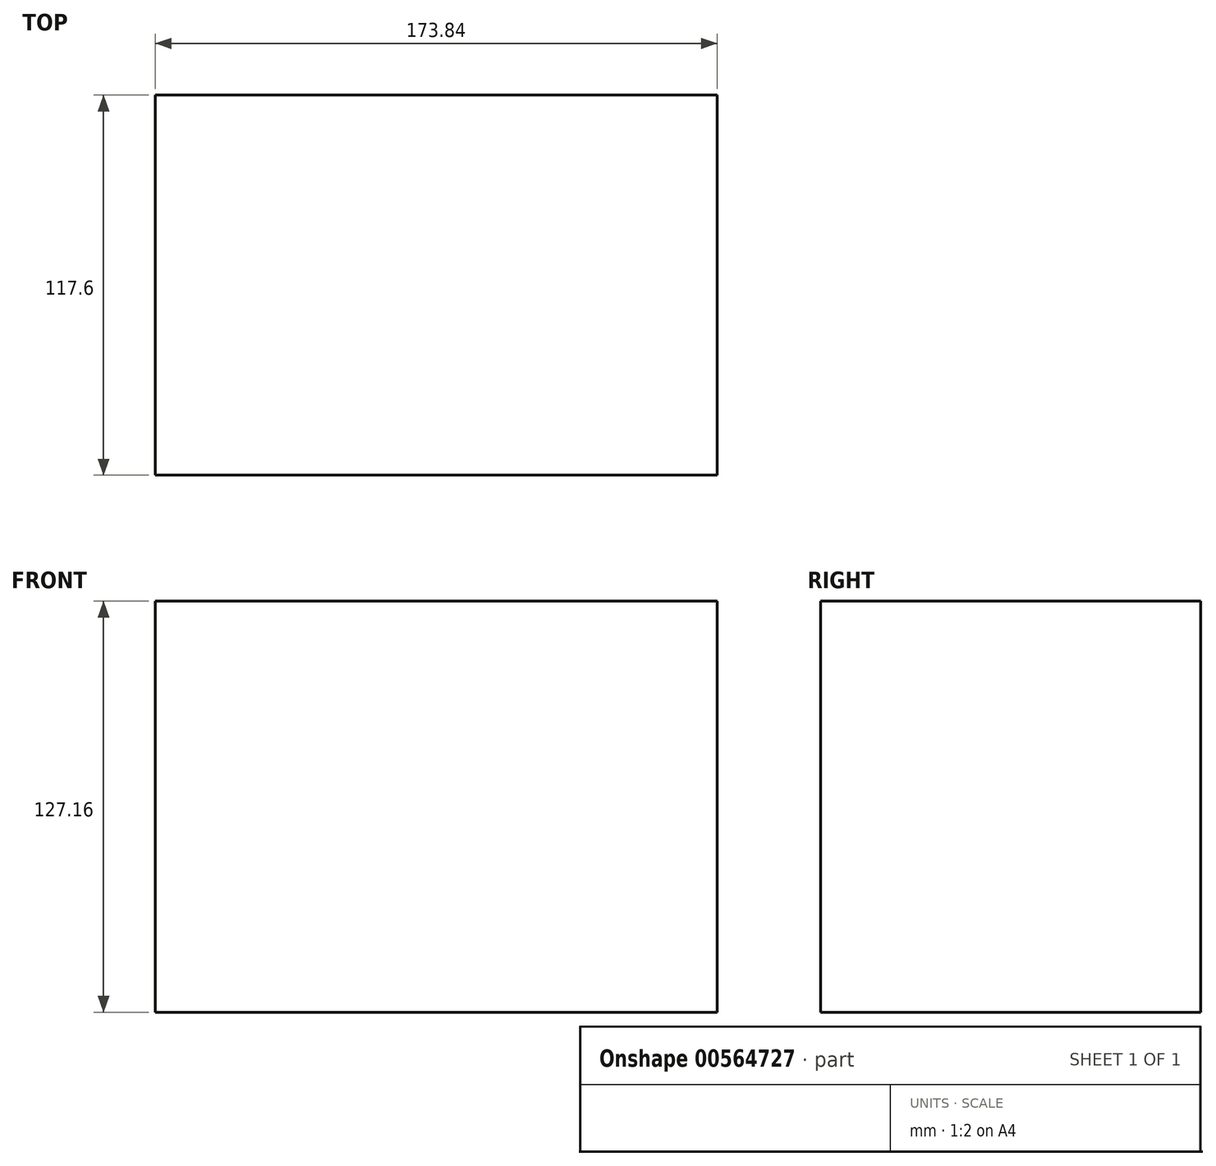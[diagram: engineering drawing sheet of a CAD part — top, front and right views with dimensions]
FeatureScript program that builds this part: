
annotation { "Feature Type Name" : "Feature", "Feature Type Description" : "" }
export const myFeature = defineFeature(function(context is Context, id is Id, definition is map)
    precondition{}
    {
        {
            var Q0;
            Q0=qCreatedBy(makeId("Front.planeOp"),FACE);
            var sketch = newSketch(context, id + "F0", { "sketchPlane" : qUnion([Q0])});
            skLineSegment(sketch, "E0.bottom", {"start": v(86.92, -63.58) * mm, "end": v(-86.92, -63.58) * mm});
            skLineSegment(sketch, "E0.top", {"start": v(86.92, 63.58) * mm, "end": v(-86.92, 63.58) * mm});
            skLineSegment(sketch, "E0.left", {"start": v(86.92, -63.58) * mm, "end": v(86.92, 63.58) * mm});
            skLineSegment(sketch, "E0.right", {"start": v(-86.92, -63.58) * mm, "end": v(-86.92, 63.58) * mm});
            skPoint(sketch, "E0.middle", {"position": v(0, 0) * mm});
            skSolve(sketch);
        }
        {
            var Q0;
            Q0 = qSketchRegion(id + "F0", true);
            extrude(context, id + "F1", {"entities" : qUnion([Q0]), "depth" : 117.6 * mm, "offsetDistance" : 25.4 * mm});
        }
    });
